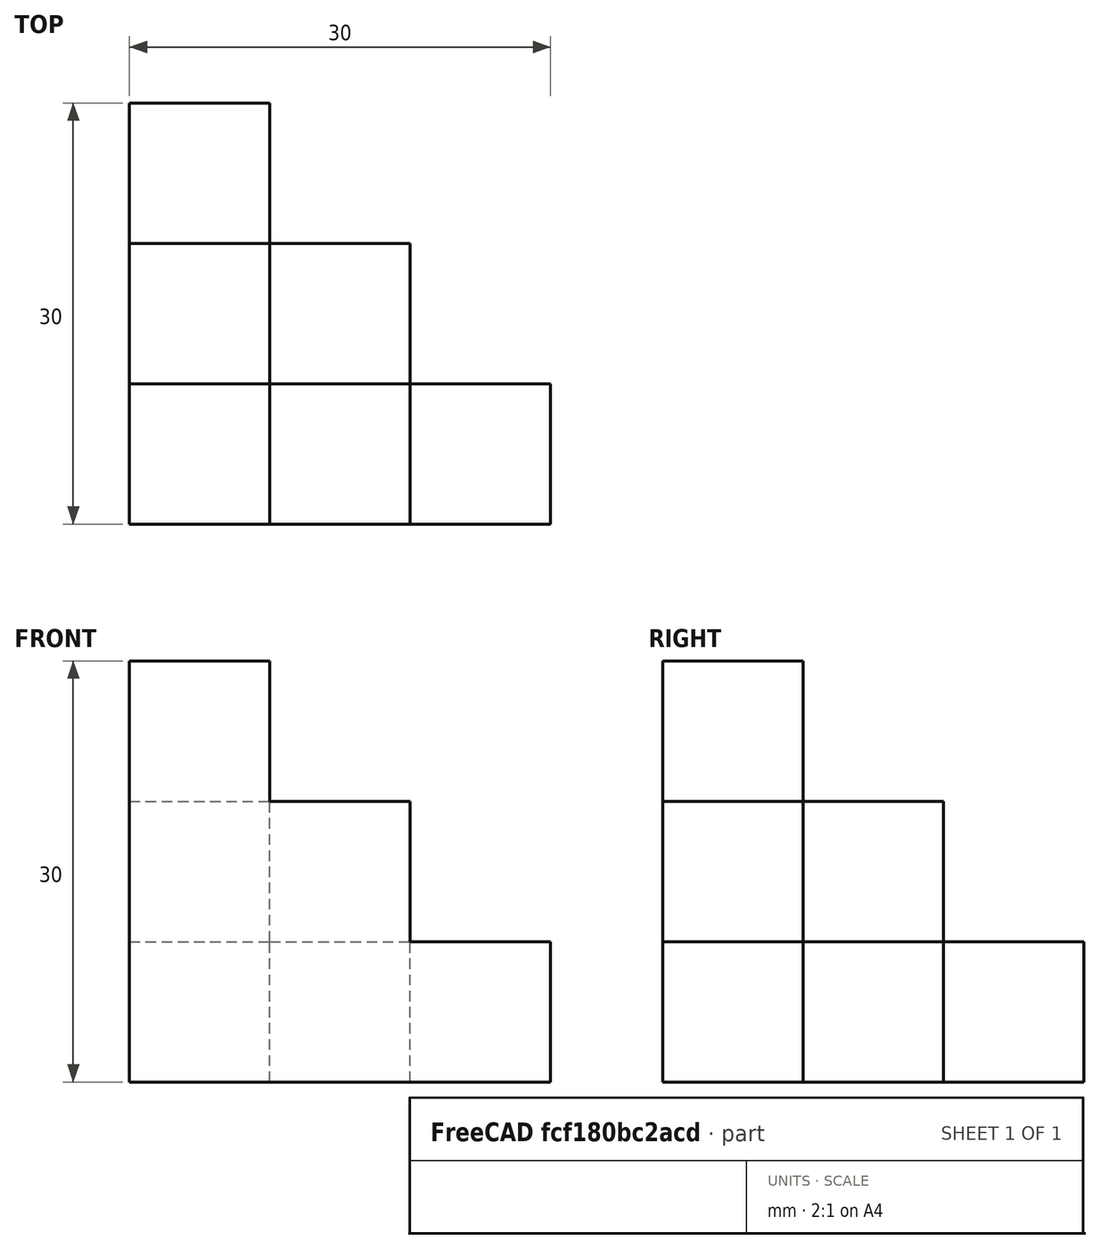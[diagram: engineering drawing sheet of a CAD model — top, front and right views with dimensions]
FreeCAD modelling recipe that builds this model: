
FCSTD DOCUMENT  (FreeCAD 0.18.4R)
Label: tutorial_freecad_ex05_b
License: All rights reserved
LicenseURL: http://en.wikipedia.org/wiki/All_rights_reserved
objects: Part::Box×6, Part::MultiFuse×1, Part::Feature×1
note: 8 computed .brp shape members not serialized (recipe doc carries the construction recipe); baked Part::Feature solids carry a one-line shape summary decoded from their .brp

FEATURE [Part::Box] Box  label="Nivel01_cubo01"
  AttacherType = Attacher::AttachEngine3D
  Height = 30
  Length = 10
  Width = 10
FEATURE [Part::Box] Box001  label="Nivel02_cubo01"
  AttacherType = Attacher::AttachEngine3D
  Height = 20
  Length = 10
  Placement = pos=(10,0,0) rot=(0,0,1;0rad)
  Width = 10
FEATURE [Part::Box] Box002  label="Nivel02_cubo02"
  AttacherType = Attacher::AttachEngine3D
  Height = 20
  Length = 10
  Placement = pos=(0,10,0) rot=(0,0,1;0rad)
  Width = 10
FEATURE [Part::Box] Box003  label="Nivel03_cubo001"
  AttacherType = Attacher::AttachEngine3D
  Height = 10
  Length = 10
  Placement = pos=(20,0,0) rot=(0,0,1;0rad)
  Width = 10
FEATURE [Part::Box] Box004  label="Nivel03_cubo002"
  AttacherType = Attacher::AttachEngine3D
  Height = 10
  Length = 10
  Placement = pos=(0,20,0) rot=(0,0,1;0rad)
  Width = 10
FEATURE [Part::Box] Box005  label="Nivel03_cubo003"
  AttacherType = Attacher::AttachEngine3D
  Height = 10
  Length = 10
  Placement = pos=(10,10,0) rot=(0,0,1;0rad)
  Width = 10
FEATURE [Part::MultiFuse] Fusion
  Refine = true
  Shapes = -> [Box,Box004,Box001,Box002,Box003,Box005]
FEATURE [Part::Feature] Fusion001
  shape: bbox 30 x 30 x 30 mm, 21 faces (baked)
